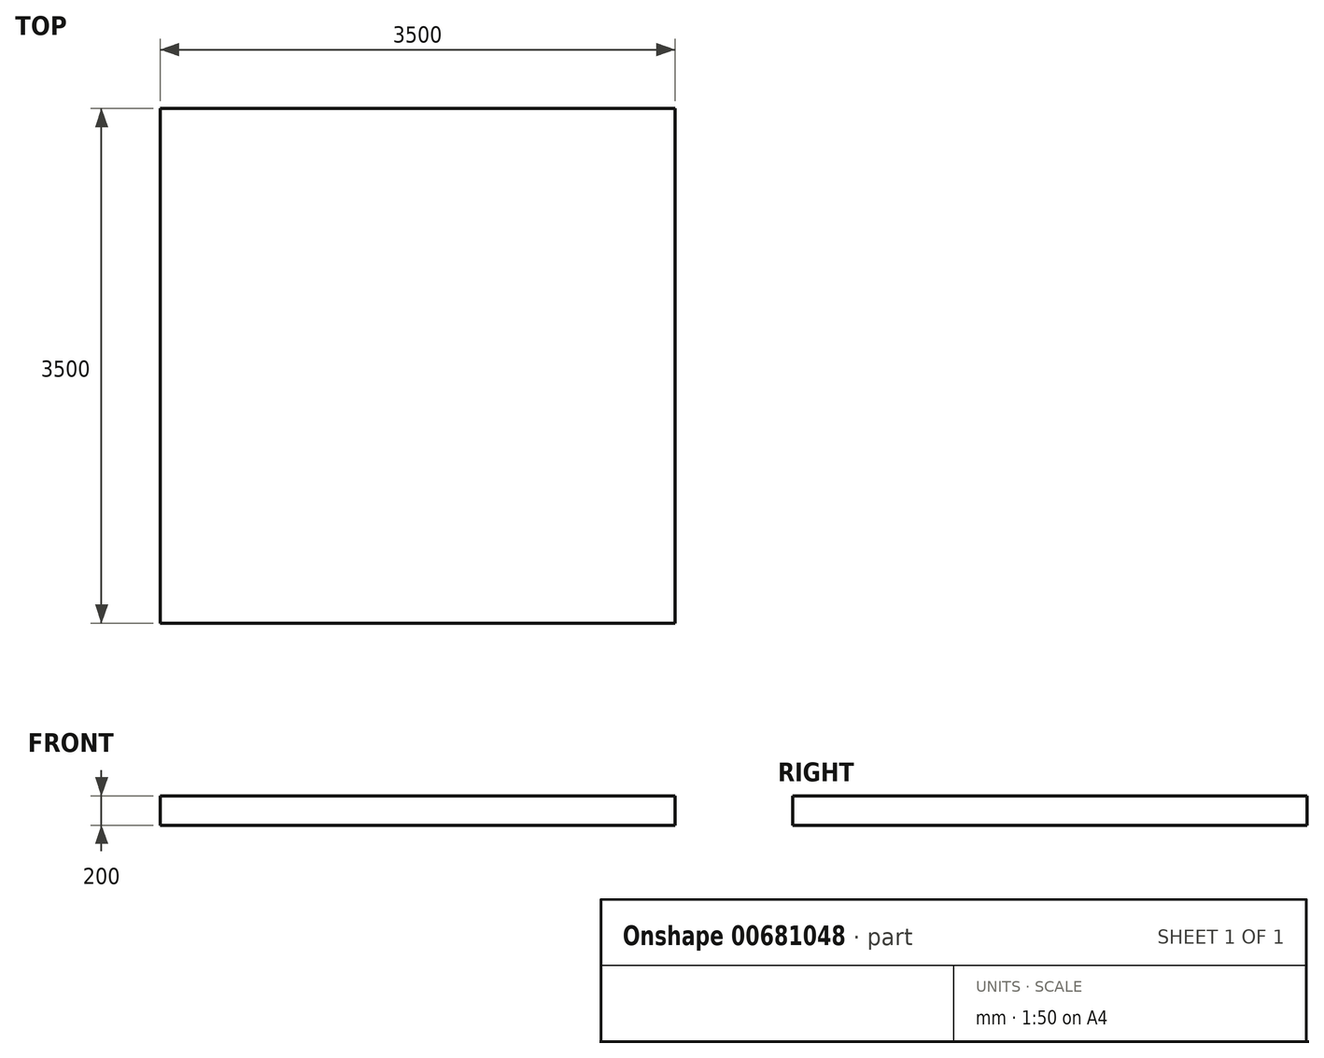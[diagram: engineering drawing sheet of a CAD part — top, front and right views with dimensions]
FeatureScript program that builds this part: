
annotation { "Feature Type Name" : "Feature", "Feature Type Description" : "" }
export const myFeature = defineFeature(function(context is Context, id is Id, definition is map)
    precondition{}
    {
        {
            var Q0;
            Q0=qCreatedBy(makeId("Top.planeOp"),FACE);
            var sketch = newSketch(context, id + "F0", { "sketchPlane" : qUnion([Q0])});
            skLineSegment(sketch, "E0.bottom", {"start": v(-1750, -1750) * mm, "end": v(1750, -1750) * mm});
            skLineSegment(sketch, "E0.top", {"start": v(-1750, 1750) * mm, "end": v(1750, 1750) * mm});
            skLineSegment(sketch, "E0.left", {"start": v(-1750, -1750) * mm, "end": v(-1750, 1750) * mm});
            skLineSegment(sketch, "E0.right", {"start": v(1750, -1750) * mm, "end": v(1750, 1750) * mm});
            skLineSegment(sketch, "E1", {"start": v(-1750, -1750) * mm, "end": v(1750, 1750) * mm, "construction": true});
            skLineSegment(sketch, "E2", {"start": v(-1750, 1750) * mm, "end": v(1750, -1750) * mm, "construction": true});
            skSolve(sketch);
        }
        {
            var Q0;
            Q0 = qSketchRegion(id + "F0", true);
            extrude(context, id + "F1", {"entities" : qUnion([Q0]), "depth" : 200 * mm, "offsetDistance" : 25 * mm});
        }
    });
